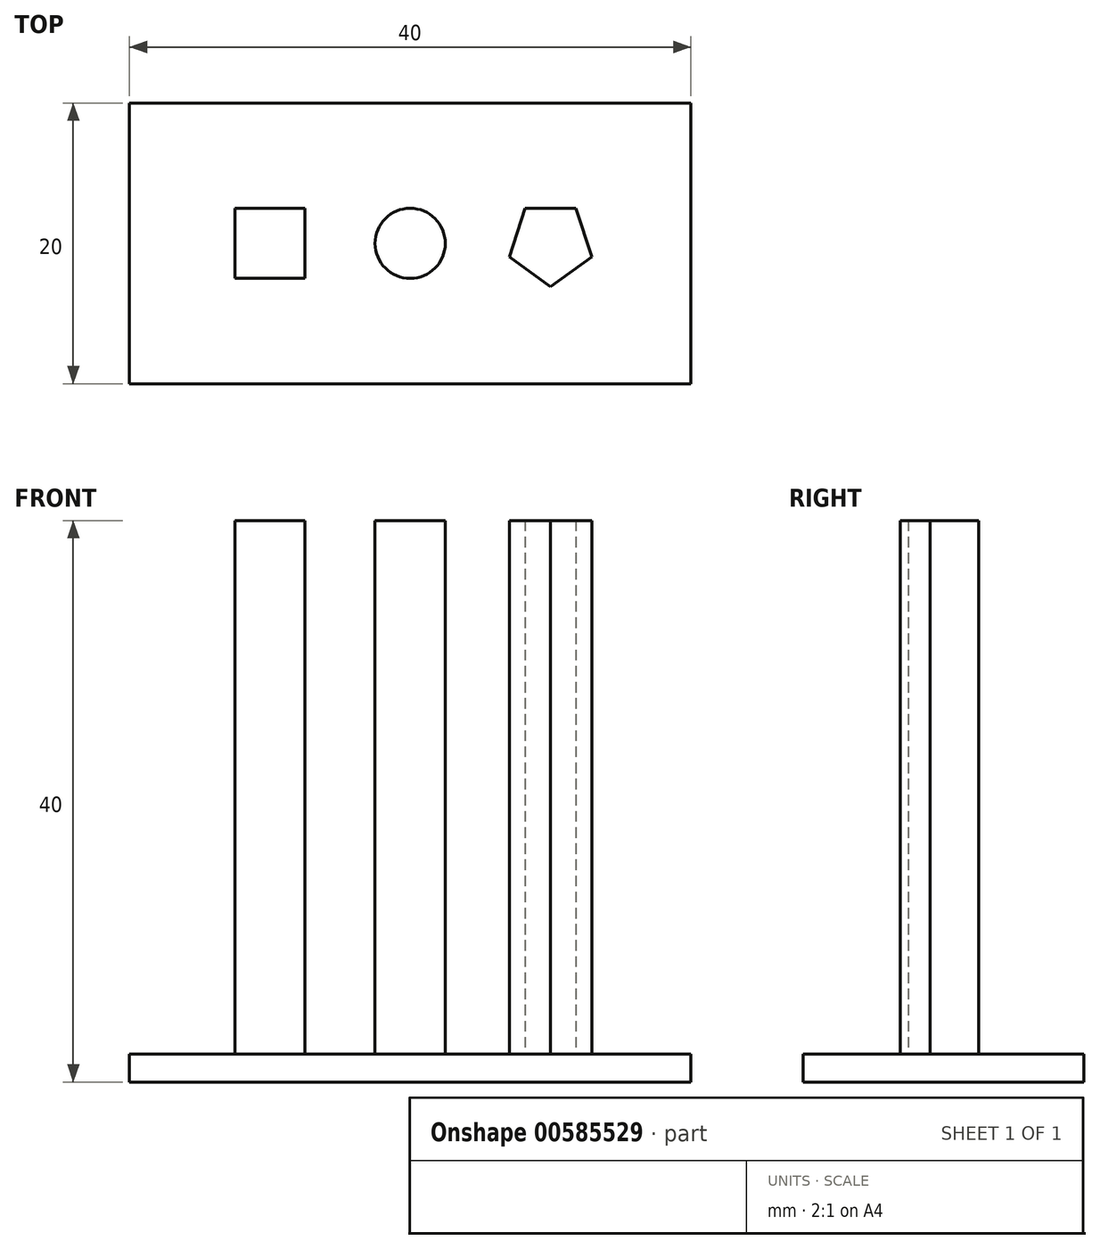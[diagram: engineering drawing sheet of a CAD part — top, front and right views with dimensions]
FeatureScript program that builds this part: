
annotation { "Feature Type Name" : "Feature", "Feature Type Description" : "" }
export const myFeature = defineFeature(function(context is Context, id is Id, definition is map)
    precondition{}
    {
        {
            var Q0;
            Q0=qCreatedBy(makeId("Top.planeOp"),FACE);
            var sketch = newSketch(context, id + "F0", { "sketchPlane" : qUnion([Q0])});
            skLineSegment(sketch, "E0.bottom", {"start": v(20, 10) * mm, "end": v(-20, 10) * mm});
            skLineSegment(sketch, "E0.top", {"start": v(20, -10) * mm, "end": v(-20, -10) * mm});
            skLineSegment(sketch, "E0.left", {"start": v(20, 10) * mm, "end": v(20, -10) * mm});
            skLineSegment(sketch, "E0.right", {"start": v(-20, 10) * mm, "end": v(-20, -10) * mm});
            skPoint(sketch, "E0.middle", {"position": v(0, 0) * mm});
            skCircle(sketch, "E1", {"center": v(0, 0) * mm, "radius": 2.5 * mm});
            skLineSegment(sketch, "E2.bottom", {"start": v(-7.5, 2.5) * mm, "end": v(-12.5, 2.5) * mm});
            skLineSegment(sketch, "E2.top", {"start": v(-7.5, -2.5) * mm, "end": v(-12.5, -2.5) * mm});
            skLineSegment(sketch, "E2.left", {"start": v(-7.5, 2.5) * mm, "end": v(-7.5, -2.5) * mm});
            skLineSegment(sketch, "E2.right", {"start": v(-12.5, 2.5) * mm, "end": v(-12.5, -2.5) * mm});
            skPoint(sketch, "E2.middle", {"position": v(-10, 0) * mm});
            skPoint(sketch, "E3", {"position": v(10, 0) * mm});
            skCircle(sketch, "E4.cCircle", {"center": v(10, 0) * mm, "radius": 2.5 * mm, "construction": true});
            skLineSegment(sketch, "E4.0", {"start": v(8.18, 2.5) * mm, "end": v(11.82, 2.5) * mm});
            skLineSegment(sketch, "E4.1", {"start": v(11.82, 2.5) * mm, "end": v(12.94, -0.95) * mm});
            skLineSegment(sketch, "E4.2", {"start": v(12.94, -0.95) * mm, "end": v(10, -3.1) * mm});
            skLineSegment(sketch, "E4.3", {"start": v(10, -3.1) * mm, "end": v(7.06, -0.95) * mm});
            skLineSegment(sketch, "E4.4", {"start": v(7.06, -0.95) * mm, "end": v(8.18, 2.5) * mm});
            skPoint(sketch, "E4.0.midPoint", {"position": v(10, 2.5) * mm});
            skSolve(sketch);
        }
        {
            var Q0;
            Q0=makeQuery(id+"F0.imprint","IMPRINT",FACE,{"disambiguationData":[TD([[makeQuery(id+"F0.imprint","IMPRINT",EDGE,{"derivedFrom":sQuery(id+"F0.wireOp",EDGE,"E2.bottom")}),1.0]])]});
            var Q1;
            Q1=makeQuery(id+"F0.imprint","IMPRINT",FACE,{"disambiguationData":[TD([[makeQuery(id+"F0.imprint","IMPRINT",EDGE,{"derivedFrom":sQuery(id+"F0.wireOp",EDGE,"E1")}),1.0]])]});
            var Q2;
            Q2=makeQuery(id+"F0.imprint","IMPRINT",FACE,{"disambiguationData":[TD([[makeQuery(id+"F0.imprint","IMPRINT",EDGE,{"derivedFrom":sQuery(id+"F0.wireOp",EDGE,"E4.0")}),-1.0]])]});
            var Q3;
            Q3=makeQuery(id+"F0.imprint","IMPRINT",FACE,{"disambiguationData":[TD([[makeQuery(id+"F0.imprint","IMPRINT",EDGE,{"derivedFrom":sQuery(id+"F0.wireOp",EDGE,"E0.bottom")}),1.0]])]});
            extrude(context, id + "F1", {"entities" : qUnion([Q0, Q1, Q2, Q3]), "depth" : 2 * mm, "offsetDistance" : 25 * mm});
        }
        {
            var Q0;
            Q0=makeQuery(id+"F0.imprint","IMPRINT",FACE,{"disambiguationData":[TD([[makeQuery(id+"F0.imprint","IMPRINT",EDGE,{"derivedFrom":sQuery(id+"F0.wireOp",EDGE,"E2.bottom")}),1.0]])]});
            var Q1;
            Q1=makeQuery(id+"F0.imprint","IMPRINT",FACE,{"disambiguationData":[TD([[makeQuery(id+"F0.imprint","IMPRINT",EDGE,{"derivedFrom":sQuery(id+"F0.wireOp",EDGE,"E1")}),1.0]])]});
            var Q2;
            Q2=makeQuery(id+"F0.imprint","IMPRINT",FACE,{"disambiguationData":[TD([[makeQuery(id+"F0.imprint","IMPRINT",EDGE,{"derivedFrom":sQuery(id+"F0.wireOp",EDGE,"E4.0")}),-1.0]])]});
            extrude(context, id + "F2", {"entities" : qUnion([Q0, Q1, Q2]), "operationType" : NewBodyOperationType.ADD, "depth" : 40 * mm, "offsetDistance" : 25 * mm});
        }
    });
